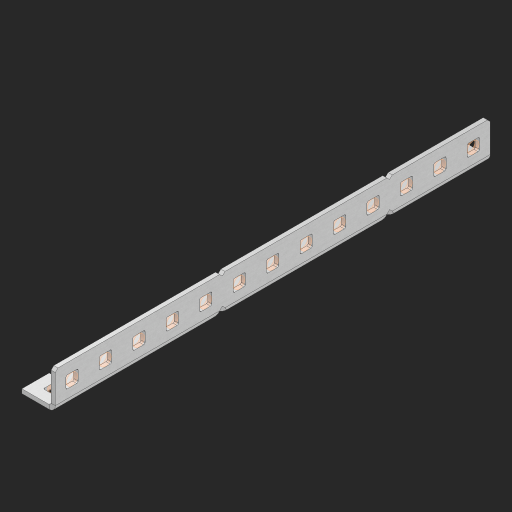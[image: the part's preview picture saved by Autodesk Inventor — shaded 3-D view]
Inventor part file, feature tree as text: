
AUTODESK INVENTOR PART (.ipt)
format: ipt  version: 2023 (Build 270158000, 158)  size: 794,112 bytes
history: native  units: in
note: dims shown in document units (in); Inventor stores cm internally (conversion verified against a paired STEP export)
features: other x187, extrude x37, sheet_metal_op x11, sketch x10, pattern_linear x2, mirror x1, chamfer x1
ambient origin geometry x8: Origin, YZ Plane, XZ Plane, XY Plane, X Axis, Y Axis, Z Axis, Center Point
bodies: Solid1 (feature_tree), Body (feature_tree)
feature tree (249):
  other  "Alu Half C 1x2x1x13"
  other  "Table"
  other  "Alu C 1x2x1x35"
  other  "Alu C 1x2x1x34"
  other  "Alu C 1x2x1x33"
  other  "Alu C 1x2x1x32"
  other  "Alu C 1x2x1x31"
  other  "Alu C 1x2x1x30"
  other  "Alu C 1x2x1x29"
  other  "Alu C 1x2x1x28"
  other  "Alu C 1x2x1x27"
  other  "Alu C 1x2x1x26"
  other  "Alu C 1x2x1x25"
  other  "Alu C 1x2x1x24"
  other  "Alu C 1x2x1x23"
  other  "Alu C 1x2x1x22"
  other  "Alu C 1x2x1x21"
  other  "Alu C 1x2x1x20"
  other  "Alu C 1x2x1x19"
  other  "Alu C 1x2x1x18"
  other  "Alu C 1x2x1x17"
  other  "Alu C 1x2x1x16"
  other  "Alu C 1x2x1x15"
  other  "Alu C 1x2x1x14"
  other  "Alu C 1x2x1x13"
  other  "Alu C 1x2x1x12"
  other  "Alu C 1x2x1x11"
  other  "Alu C 1x2x1x10"
  other  "Alu C 1x2x1x9"
  other  "Alu C 1x2x1x8"
  other  "Alu C 1x2x1x7"
  other  "Alu C 1x2x1x6"
  other  "Alu C 1x2x1x5"
  other  "Alu C 1x2x1x4"
  other  "Alu C 1x2x1x3"
  other  "Alu C 1x2x1x2"
  other  "Alu C 1x2x1x1"
  other  "Steel C 1x2x1x35"
  other  "Steel C 1x2x1x34"
  other  "Steel C 1x2x1x33"
  other  "Steel C 1x2x1x32"
  other  "Steel C 1x2x1x31"
  other  "Steel C 1x2x1x30"
  other  "Steel C 1x2x1x29"
  other  "Steel C 1x2x1x28"
  other  "Steel C 1x2x1x27"
  other  "Steel C 1x2x1x26"
  other  "Steel C 1x2x1x25"
  other  "Steel C 1x2x1x24"
  other  "Steel C 1x2x1x23"
  other  "Steel C 1x2x1x22"
  other  "Steel C 1x2x1x21"
  other  "Steel C 1x2x1x20"
  other  "Steel C 1x2x1x19"
  other  "Steel C 1x2x1x18"
  other  "Steel C 1x2x1x17"
  other  "Steel C 1x2x1x16"
  other  "Steel C 1x2x1x15"
  other  "Steel C 1x2x1x14"
  other  "Steel C 1x2x1x13"
  other  "Steel C 1x2x1x12"
  other  "Steel C 1x2x1x11"
  other  "Steel C 1x2x1x10"
  other  "Steel C 1x2x1x9"
  other  "Steel C 1x2x1x8"
  other  "Steel C 1x2x1x7"
  other  "Steel C 1x2x1x6"
  other  "Steel C 1x2x1x5"
  other  "Steel C 1x2x1x4"
  other  "Steel C 1x2x1x3"
  other  "Steel C 1x2x1x2"
  other  "Steel C 1x2x1x1"
  other  "Alu Half C 1x2x1x35"
  other  "Alu Half C 1x2x1x34"
  other  "Alu Half C 1x2x1x33"
  other  "Alu Half C 1x2x1x32"
  other  "Alu Half C 1x2x1x31"
  other  "Alu Half C 1x2x1x30"
  other  "Alu Half C 1x2x1x29"
  other  "Alu Half C 1x2x1x28"
  other  "Alu Half C 1x2x1x27"
  other  "Alu Half C 1x2x1x26"
  other  "Alu Half C 1x2x1x25"
  other  "Alu Half C 1x2x1x24"
  other  "Alu Half C 1x2x1x23"
  other  "Alu Half C 1x2x1x22"
  other  "Alu Half C 1x2x1x21"
  other  "Alu Half C 1x2x1x20"
  other  "Alu Half C 1x2x1x19"
  other  "Alu Half C 1x2x1x18"
  other  "Alu Half C 1x2x1x17"
  other  "Alu Half C 1x2x1x16"
  other  "Alu Half C 1x2x1x15"
  other  "Alu Half C 1x2x1x14"
  other  "Alu Half C 1x2x1x12"
  other  "Alu Half C 1x2x1x11"
  other  "Alu Half C 1x2x1x10"
  other  "Alu Half C 1x2x1x9"
  other  "Alu Half C 1x2x1x8"
  other  "Alu Half C 1x2x1x7"
  other  "Alu Half C 1x2x1x6"
  other  "Alu Half C 1x2x1x5"
  other  "Alu Half C 1x2x1x4"
  other  "Alu Half C 1x2x1x3"
  other  "Alu Half C 1x2x1x2"
  other  "Alu Half C 1x2x1x1"
  other  "Steel Half C 1x2x1x35"
  other  "Steel Half C 1x2x1x34"
  other  "Steel Half C 1x2x1x33"
  other  "Steel Half C 1x2x1x32"
  other  "Steel Half C 1x2x1x31"
  other  "Steel Half C 1x2x1x30"
  other  "Steel Half C 1x2x1x29"
  other  "Steel Half C 1x2x1x28"
  other  "Steel Half C 1x2x1x27"
  other  "Steel Half C 1x2x1x26"
  other  "Steel Half C 1x2x1x25"
  other  "Steel Half C 1x2x1x24"
  other  "Steel Half C 1x2x1x23"
  other  "Steel Half C 1x2x1x22"
  other  "Steel Half C 1x2x1x21"
  other  "Steel Half C 1x2x1x20"
  other  "Steel Half C 1x2x1x19"
  other  "Steel Half C 1x2x1x18"
  other  "Steel Half C 1x2x1x17"
  other  "Steel Half C 1x2x1x16"
  other  "Steel Half C 1x2x1x15"
  other  "Steel Half C 1x2x1x14"
  other  "Steel Half C 1x2x1x13"
  other  "Steel Half C 1x2x1x12"
  other  "Steel Half C 1x2x1x11"
  other  "Steel Half C 1x2x1x10"
  other  "Steel Half C 1x2x1x9"
  other  "Steel Half C 1x2x1x8"
  other  "Steel Half C 1x2x1x7"
  other  "Steel Half C 1x2x1x6"
  other  "Steel Half C 1x2x1x5"
  other  "Steel Half C 1x2x1x4"
  other  "Steel Half C 1x2x1x3"
  other  "Steel Half C 1x2x1x2"
  other  "Steel Half C 1x2x1x1"
  sheet_metal_op  "Flanges"
  other  "Flange Pattern Plane"
  other  "Flange Pattern Sketch"
  sheet_metal_op  "Flange Pattern"
  sheet_metal_op  "Body Pattern"
  pattern_linear  "Center Pattern"  Spacing1=0.0625in  [1 undecoded]
  other  "Arc Length"
  mirror  "Notch Mirror"
  pattern_linear  "Notch Pattern"  Spacing1=0.182in  [1 undecoded]
  chamfer  "End Chamfer"
  extrude  "Half Cut"  Depth=0.02in
  sketch  "Sketch1"  dims[d0=1.0in]
  other  "Plate1"
  sketch  "Sketch2"  dims[d1=6.5in]
  other  "Plate2"
  sheet_metal_op  "Bend1"
  sheet_metal_op  "Corner1"
  sketch  "Sketch3"  dims[d2=0.0625in]
  sketch  "Sketch7"  dims[d3=0.0625in]
  other  "Srf1"
  other  "Srf2"
  sketch  "Sketch8"  dims[d4=0.0312in]
  sketch  "Sketch9"  dims[d5=0.125in]
  other  "Srf91"
  sheet_metal_op  "Body Pattern Sketch"
  other  "Srf92"
  sketch  "Sketch13"  dims[d6=0.0625in]
  sketch  "Sketch14"  dims[d7=0.5in d8=90.0deg d9=0.0312in]
  sketch  "Sketch15"  dims[d10=0.25in]
  sketch  "Sketch16"  dims[d11=0.0625in d12=0.0625in d16=0.182in d17=0.02in d18=0.0625in d19=0.0in d20=0.25in d21=0.25in d38=5.1181in d40=0.5in d41=0.3937in d43=1.0in d46=0.172in d47=1.0in d48=0.0in d49=0.182in d50=0.02in d51=0.25in d52=0.25in d53=0.0625in d54=0.0in d55=0.172in d56=1.0in d57=0.0in d58=0.25in d60=5.1181in d62=0.5in d63=0.3937in d65=0.5in d85=0.1473in d86=0.1782in d88=0.04in d89=0.0625in d90=0.0in d91=0.04in d92=0.0491in d95=2.5in d96=0.04in d97=0.25in d98=45.0deg d99=0.25in d100=0.5in d101=0.0in d102=2.497in d106=0.182in d107=0.02in d108=0.5in d109=0.5in d110=0.0625in d111=0.0in d112=0.172in d113=0.5in d114=0.0in d117=0.5in d118=0.5in d119=0.5in]
  other  "Srf786"
  other  "Srf823"
  other  "Srf824"
  other  "Srf825"
  other  "Srf826"
  other  "Srf827"
  other  "Srf828"
  other  "Srf829"
  other  "Srf856"
  other  "Srf857"
  other  "Srf858"
  other  "Srf859"
  other  "Srf860"
  other  "Srf861"
  other  "Srf862"
  other  "Srf889"
  other  "Srf890"
  other  "Srf891"
  other  "Srf892"
  other  "Srf893"
  other  "Srf894"
  other  "Srf895"
  other  "Srf896"
  other  "Srf922"
  other  "Srf923"
  other  "Srf924"
  other  "Srf925"
  other  "Srf959"
  other  "Srf960"
  other  "Srf961"
  other  "Srf962"
  other  "Srf996"
  other  "Srf997"
  other  "Srf998"
  other  "Srf999"
  sheet_metal_op  "Flange Stamp"
  sheet_metal_op  "Flange Circle"
  sheet_metal_op  "Body Stamp"
  sheet_metal_op  "Body Circle"
  other  "Center Stamp"
  other  "Center Circle"
  sheet_metal_op  "Notch"
  extrude  "ExtrusionSrf2"  Depth=0.0625in
  extrude  "ExtrusionSrf92"  TaperAngle=0.0deg  [1 undecoded]
  extrude  "ExtrusionSrf823"  Depth=0.5in
  extrude  "ExtrusionSrf824"  Depth=0.5in
  extrude  "ExtrusionSrf825"  Depth=0.5in
  extrude  "ExtrusionSrf826"  Depth=0.5in
  extrude  "ExtrusionSrf827"  Depth=1.0in TaperAngle=0.0deg
  extrude  "ExtrusionSrf828"  Depth=0.182in
  extrude  "ExtrusionSrf829"  Depth=0.02in
  extrude  "ExtrusionSrf856"  Depth=0.5in
  extrude  "ExtrusionSrf857"  Depth=0.5in
  extrude  "ExtrusionSrf858"  Depth=0.0625in
  extrude  "ExtrusionSrf859"  TaperAngle=0.0deg  [1 undecoded]
  extrude  "ExtrusionSrf860"  Depth=0.5in
  extrude  "ExtrusionSrf861"  Depth=1.0in TaperAngle=0.0deg
  extrude  "ExtrusionSrf862"  Depth=0.5in
  extrude  "ExtrusionSrf889"  Depth=0.5in
  extrude  "ExtrusionSrf890"  Depth=0.5in
  extrude  "ExtrusionSrf891"  Depth=0.5in
  extrude  "ExtrusionSrf892"  Depth=0.5in
  extrude  "ExtrusionSrf893"  Depth=0.5in
  extrude  "ExtrusionSrf894"  Depth=0.0625in
  extrude  "ExtrusionSrf895"  TaperAngle=0.0deg  [1 undecoded]
  extrude  "ExtrusionSrf896"  Depth=0.5in
  extrude  "ExtrusionSrf922"  Depth=0.5in
  extrude  "ExtrusionSrf923"  Depth=2.5in
  extrude  "ExtrusionSrf924"  Depth=0.5in TaperAngle=45.0deg
  extrude  "ExtrusionSrf925"  Depth=0.5in
  extrude  "ExtrusionSrf959"  Depth=0.5in TaperAngle=0.0deg
  extrude  "ExtrusionSrf960"  Depth=0.5in
  extrude  "ExtrusionSrf961"  Depth=0.182in
  extrude  "ExtrusionSrf962"  Depth=0.02in
  extrude  "ExtrusionSrf996"  Depth=0.5in
  extrude  "ExtrusionSrf997"  Depth=0.5in
  extrude  "ExtrusionSrf998"  Depth=0.0625in
  extrude  "ExtrusionSrf999"  TaperAngle=0.0deg  [1 undecoded]
note: 6 required parameter values undecoded (feature->parameter linkage not recoverable at this tier; creation-order binding heuristic only, values carry confidence <= 0.55)
